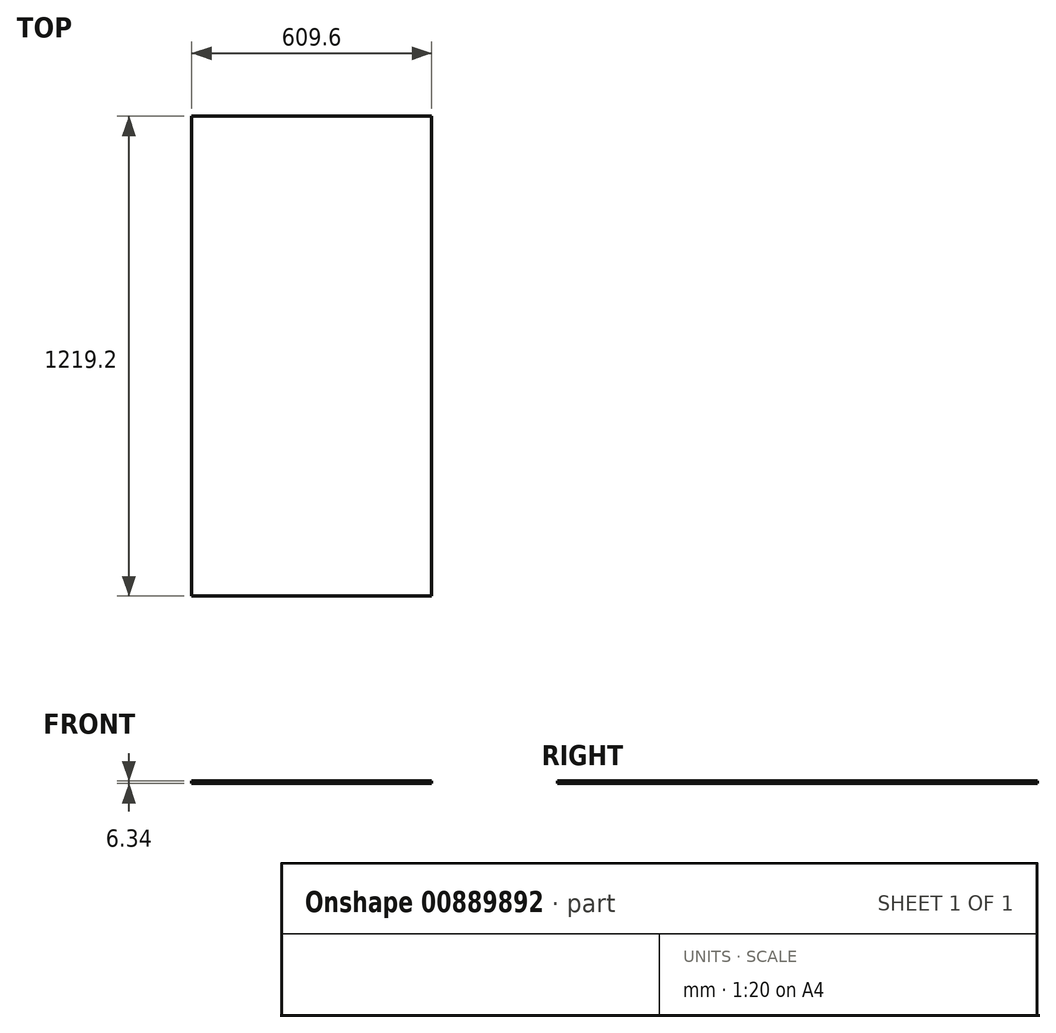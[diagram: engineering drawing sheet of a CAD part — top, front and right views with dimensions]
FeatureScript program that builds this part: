
annotation { "Feature Type Name" : "Feature", "Feature Type Description" : "" }
export const myFeature = defineFeature(function(context is Context, id is Id, definition is map)
    precondition{}
    {
        {
            var Q0;
            Q0=qCreatedBy(makeId("Front.planeOp"),FACE);
            var sketch = newSketch(context, id + "F0", { "sketchPlane" : qUnion([Q0])});
            skLineSegment(sketch, "E0.bottom", {"start": v(304.8, -3.17) * mm, "end": v(-304.8, -3.18) * mm});
            skLineSegment(sketch, "E0.top", {"start": v(304.8, 3.18) * mm, "end": v(-304.8, 3.18) * mm});
            skLineSegment(sketch, "E0.left", {"start": v(304.8, -3.17) * mm, "end": v(304.8, 3.18) * mm});
            skLineSegment(sketch, "E0.right", {"start": v(-304.8, -3.18) * mm, "end": v(-304.8, 3.17) * mm});
            skPoint(sketch, "E0.middle", {"position": v(0, 0) * mm});
            skSolve(sketch);
        }
        {
            var Q0;
            Q0 = qSketchRegion(id + "F0", true);
            extrude(context, id + "F1", {"entities" : qUnion([Q0]), "depth" : 1219.2 * mm, "offsetDistance" : 25.4 * mm});
        }
    });
